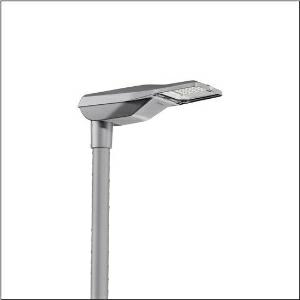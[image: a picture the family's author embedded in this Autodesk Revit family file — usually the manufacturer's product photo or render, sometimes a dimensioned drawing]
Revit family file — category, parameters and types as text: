
# Revit family: streetlight_sl_21_iq_micro___st1_0a_5xe1d31d08cb_abfe
name_source: partatom
category: Lighting Fixtures
units: mm (PartAtom-declared; Revit-internal decimal feet)

## family parameters
Cut with Voids When Loaded = No
Host = Face
Light Source = No
Part Type = Normal
Room Calculation Point = No
Round Connector Dimension = Use Diameter
Shared = No

## types (1)
- --- (1 x LED, 2870 lm, 19.4 W, 3000K)
    Apparent Load = 19 VA
    CIE Flux Codes = 37 72 97 100 100
    Color Rendering = 70
    Color Temperature = 3000K
    Default Elevation = 1800 mm
    Description = Streetlight SL 21 iQ micro, mast luminaire, primary light control with lens, of PMMA, primary optical cover: cover, of toughened safety glass, transparent, light distribution: ST1.0a, light emission: direct distribution, primary light characteristic: asymmetric, installation type: post-top, side-entry, LED, High Power LED, rated luminous flux: 2.870lm, luminous efficacy: 148lm/W, light colour: 730, colour temperature: 3000K, control gear: iQ-Comfort, control: Auto-Match, Temp-Guard, Lumen-Switch, Night-Set, Smart-Wire, Light-Fading, Desk-Remote (wireless, voltage-free reading and setting of iQ features in the workshop via application-optimized NFC function/RFID function), optimised constant luminous flux control (CLO 2.0), pre-setting: linear dimming characteristic, mains connection: 220..240V, AC, 50/60Hz, start of lifetime: 19W, end of service life: 20W, reduction: 10W, luminaire housing, of diecast aluminium, powder-coated, SITECO metallic grey (DB 702S), corrosivity category C5 high according to DIN EN ISO 12944, please order mast flange separately, inclination adjustable: 0°, 5°, 10°, 15°, sealing non-destructively replaceable, multi-level sealing system, length: 528mm, width: 235mm, height: 110mm, mast flange for spigot size: 42mm (side-entry): 5XC10008XM4, 60/48mm (side-entry/post-top): 5XC10108XM2, 76/60mm (side-entry/post-top): 5XC10108XM1, protection rating (complete): IP66, insulation class (complete): insulation class II (safety insulation), certification: CE, ENEC, ENEC+, VDE, impact resistance: IK10, permissible operating ambient temperature for outdoor applications: -40..+50°C, standard-compliant lighting for roads and squares, packaging unit: 1 piece

Light Distribution: ST1.0a
    Height = 110 mm
    Lamp = 1 x LED
    Lamp Light Flux = 2870 lm
    Lamp Power = 19.4 W
    Lamp count = 1
    Length = 528 mm
    Luminous efficacy = 148 lm/W
    Manufacturer = Siteco
    ModVariant = No
    Model = 5XE1D31D08CB
    Number of Poles = 1
    OnlyDefault = Yes
    Power Factor = 1
    Product Name = Streetlight SL 21 iQ micro | ST1.0a
    Product group = mast luminaire | pylon top
    ProductGroupID = 6100
    Protection Class = Protection class II
    Protection Degree = IP 66
    RLX_Detail_Level = 1
    RLX_Emergency_Light_Flux = 0 lm
    RLX_Emergency_Type = 0
    RLX_Emergency_Type_DB = No
    RlxData = <blob elided: 99621 chars, md5=f0b61c9a>
    Socket = socket
    Standby Power = 0 W
    System Light Flux = 2870 lm
    System Power = 19 W
    Type Comments = factory setting: luminous flux: 100 % | dim-lin: 254 | 387 mA
    Type Image = l_1006881.jpg
    URL = http://relux.com
    VarID = @adj_138783
    Voltage = 0 V
    Weight = 0.00 kg
    Width = 235 mm

## geometry (parser evidence)
native form markers: Blend x4, Sweep x12
no freeform markers — native parametric forms only
